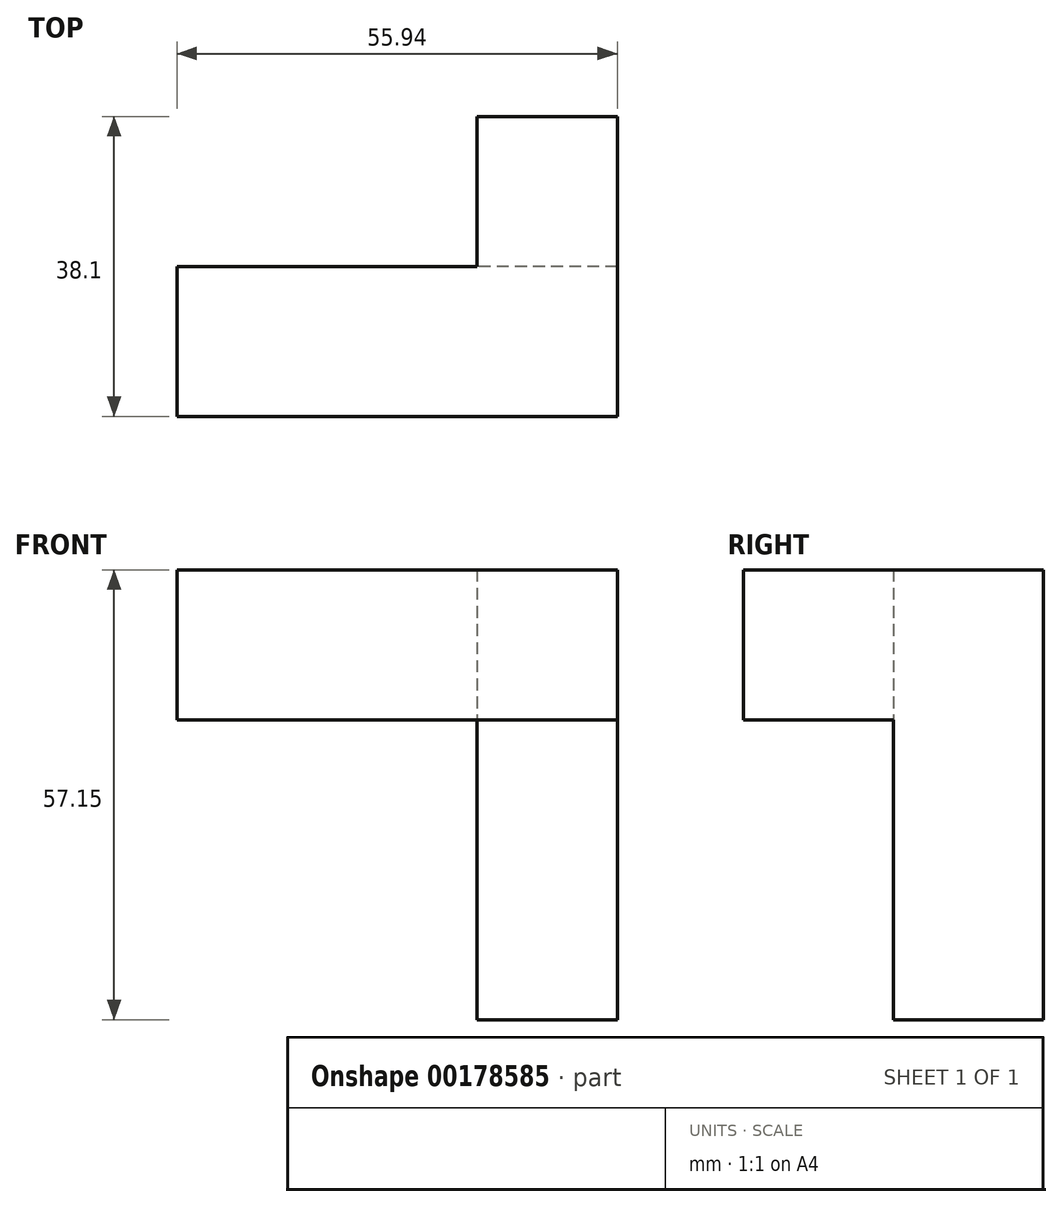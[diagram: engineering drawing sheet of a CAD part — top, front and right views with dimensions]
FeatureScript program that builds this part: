
annotation { "Feature Type Name" : "Feature", "Feature Type Description" : "" }
export const myFeature = defineFeature(function(context is Context, id is Id, definition is map)
    precondition{}
    {
        {
            var Q0;
            Q0=qCreatedBy(makeId("Front.planeOp"),FACE);
            var sketch = newSketch(context, id + "F0", { "sketchPlane" : qUnion([Q0])});
            skLineSegment(sketch, "E0", {"start": v(33.71, 46.95) * mm, "end": v(33.71, 27.9) * mm});
            skLineSegment(sketch, "E1", {"start": v(33.71, 27.9) * mm, "end": v(51.55, 27.9) * mm});
            skLineSegment(sketch, "E2", {"start": v(51.55, 27.9) * mm, "end": v(51.55, 46.95) * mm});
            skLineSegment(sketch, "E3", {"start": v(51.55, 46.95) * mm, "end": v(33.71, 46.95) * mm});
            skLineSegment(sketch, "E4", {"start": v(33.71, 27.9) * mm, "end": v(33.71, 8.85) * mm});
            skLineSegment(sketch, "E5", {"start": v(33.71, 8.85) * mm, "end": v(51.55, 8.85) * mm});
            skLineSegment(sketch, "E6", {"start": v(51.55, 8.85) * mm, "end": v(51.55, 27.9) * mm});
            skLineSegment(sketch, "E7", {"start": v(51.55, -10.2) * mm, "end": v(33.71, -10.2) * mm});
            skLineSegment(sketch, "E8", {"start": v(33.71, -10.2) * mm, "end": v(33.71, 8.85) * mm});
            skLineSegment(sketch, "E9", {"start": v(51.55, 8.85) * mm, "end": v(51.55, -10.2) * mm});
            skSolve(sketch);
        }
        {
            var Q0;
            Q0 = qSketchRegion(id + "F0", true);
            extrude(context, id + "F1", {"entities" : qUnion([Q0]), "depth" : 19.05 * mm});
        }
        {
            var Q0;
            Q0=makeQuery(id+"F1.opExtrude","CAP_FACE",FACE,{"disambiguationData":[OSD([sQuery(id+"F0.wireOp",EDGE,"E0"),sQuery(id+"F0.wireOp",EDGE,"E2"),sQuery(id+"F0.wireOp",EDGE,"E3"),sQuery(id+"F0.wireOp",EDGE,"E4"),sQuery(id+"F0.wireOp",EDGE,"E6"),sQuery(id+"F0.wireOp",EDGE,"E7"),sQuery(id+"F0.wireOp",EDGE,"E8"),sQuery(id+"F0.wireOp",EDGE,"E9")])],"isStart":false});
            var sketch = newSketch(context, id + "F2", { "sketchPlane" : qUnion([Q0])});
            skLineSegment(sketch, "E10", {"start": v(51.55, 46.95) * mm, "end": v(51.55, 27.9) * mm});
            skLineSegment(sketch, "E11", {"start": v(51.55, 27.9) * mm, "end": v(33.71, 27.9) * mm});
            skLineSegment(sketch, "E12", {"start": v(33.71, 27.9) * mm, "end": v(33.71, 46.95) * mm});
            skLineSegment(sketch, "E13", {"start": v(33.71, 46.95) * mm, "end": v(51.55, 46.95) * mm});
            skLineSegment(sketch, "E14", {"start": v(14.66, 46.95) * mm, "end": v(14.66, 27.9) * mm});
            skLineSegment(sketch, "E15", {"start": v(14.66, 27.9) * mm, "end": v(33.71, 27.9) * mm});
            skLineSegment(sketch, "E16", {"start": v(33.71, 46.95) * mm, "end": v(14.66, 46.95) * mm});
            skLineSegment(sketch, "E17", {"start": v(-4.39, 46.95) * mm, "end": v(-4.39, 27.9) * mm});
            skLineSegment(sketch, "E18", {"start": v(-4.39, 27.9) * mm, "end": v(14.66, 27.9) * mm});
            skLineSegment(sketch, "E19", {"start": v(14.66, 46.95) * mm, "end": v(-4.39, 46.95) * mm});
            skSolve(sketch);
        }
        {
            var Q0;
            Q0 = qSketchRegion(id + "F2", true);
            extrude(context, id + "F3", {"entities" : qUnion([Q0]), "operationType" : NewBodyOperationType.ADD, "depth" : 19.05 * mm});
        }
    });
